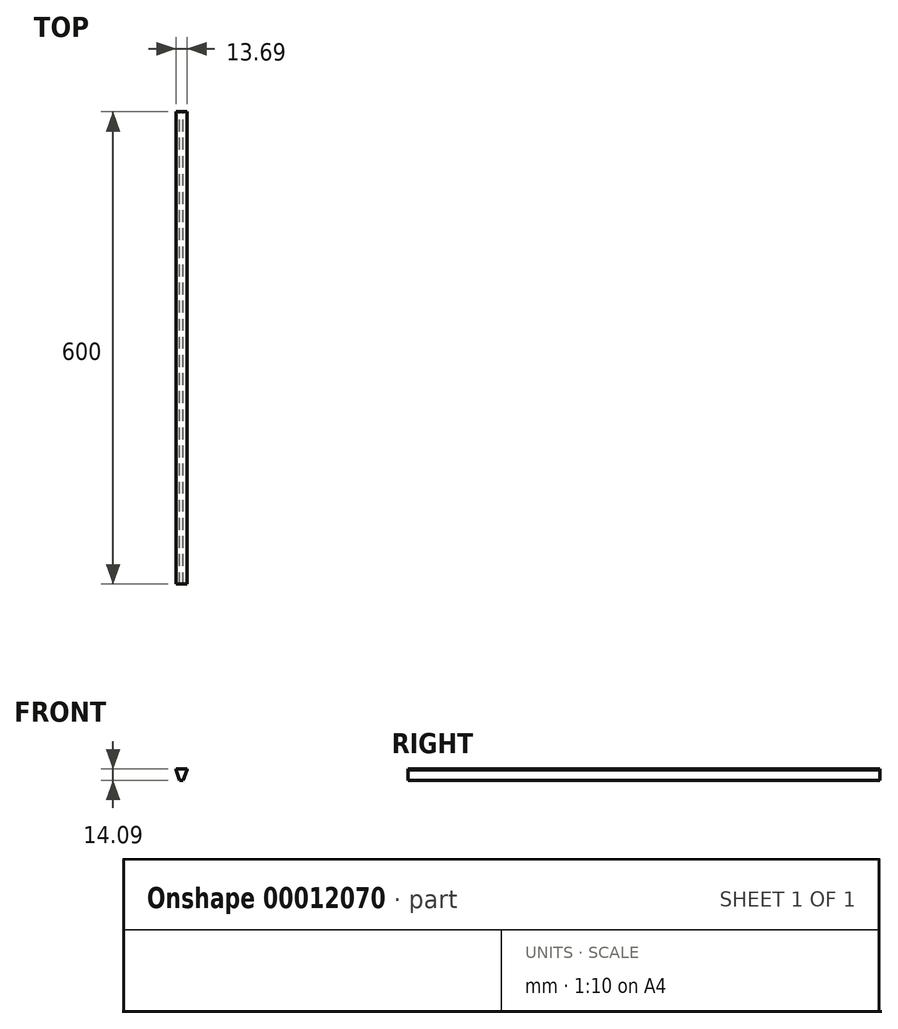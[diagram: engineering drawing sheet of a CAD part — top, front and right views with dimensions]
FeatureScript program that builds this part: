
annotation { "Feature Type Name" : "Feature", "Feature Type Description" : "" }
export const myFeature = defineFeature(function(context is Context, id is Id, definition is map)
    precondition{}
    {
        {
            var Q0;
            Q0=qCreatedBy(makeId("Front.planeOp"),FACE);
            var sketch = newSketch(context, id + "F0", { "sketchPlane" : qUnion([Q0])});
            skLineSegment(sketch, "E0", {"start": v(-1.86, -24.22) * mm, "end": v(2.44, -24.22) * mm});
            skLineSegment(sketch, "E1", {"start": v(-1.86, -24.22) * mm, "end": v(-6.56, -11.32) * mm});
            skLineSegment(sketch, "E2", {"start": v(2.44, -24.22) * mm, "end": v(7.13, -11.32) * mm});
            skPoint(sketch, "E3.start.orphan", {"position": v(0.29, -24.22) * mm});
            skPoint(sketch, "E4.orphan", {"position": v(0.29, -11.32) * mm});
            skLineSegment(sketch, "E5", {"start": v(-6.56, -10.13) * mm, "end": v(7.13, -10.13) * mm});
            skLineSegment(sketch, "E6", {"start": v(-6.56, -11.32) * mm, "end": v(-6.56, -10.13) * mm});
            skLineSegment(sketch, "E7", {"start": v(7.13, -10.13) * mm, "end": v(7.13, -11.32) * mm});
            skPoint(sketch, "E8.start.orphan", {"position": v(-7.71, -11.32) * mm});
            skPoint(sketch, "E9.trimOffspring.end.orphan", {"position": v(8.29, -11.32) * mm});
            skSolve(sketch);
        }
        {
            var Q0;
            Q0 = qSketchRegion(id + "F0", true);
            extrude(context, id + "F1", {"entities" : qUnion([Q0]), "depth" : 600 * mm});
        }
    });
